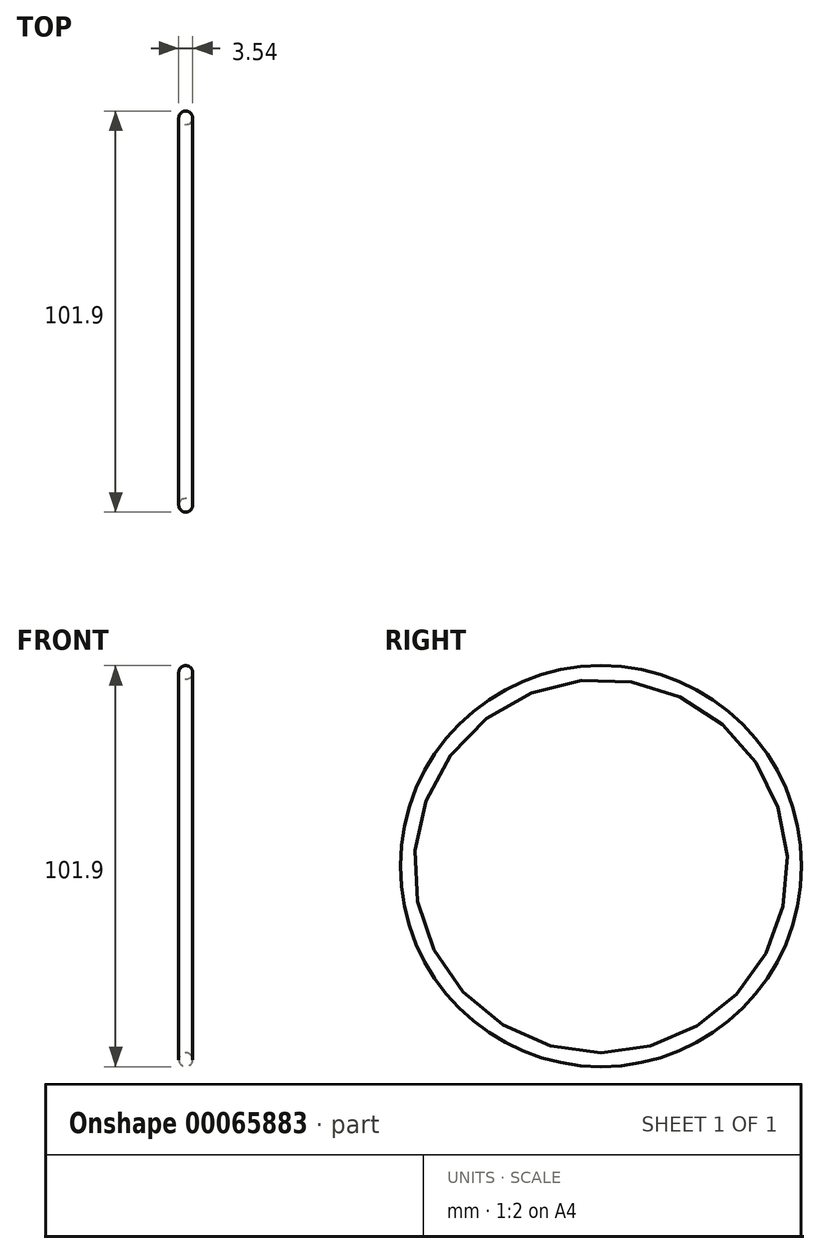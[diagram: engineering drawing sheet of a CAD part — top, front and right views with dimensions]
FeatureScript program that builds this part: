
annotation { "Feature Type Name" : "Feature", "Feature Type Description" : "" }
export const myFeature = defineFeature(function(context is Context, id is Id, definition is map)
    precondition{}
    {
        {
            var Q0;
            Q0=qCreatedBy(makeId("Front.planeOp"),FACE);
            var sketch = newSketch(context, id + "F0", { "sketchPlane" : qUnion([Q0])});
            skLineSegment(sketch, "E0", {"start": v(0, 0) * mm, "end": v(-6.06, 0) * mm, "construction": true});
            skCircle(sketch, "E1", {"center": v(0, 49.19) * mm, "radius": 1.77 * mm});
            skSolve(sketch);
        }
        {
            var Q0;
            Q0=makeQuery(id+"F0.imprint","IMPRINT",FACE,{"disambiguationData":[TD([[makeQuery(id+"F0.imprint","IMPRINT",EDGE,{"derivedFrom":sQuery(id+"F0.wireOp",EDGE,"E1")}),1.0]])]});
            var Q1;
            Q1=sQuery(id+"F0.wireOp",EDGE,"E0");
            revolve(context, id + "F1", {"entities" : qUnion([Q0]), "axis" : qUnion([Q1]), "revolveType" : RevolveType.FULL});
        }
    });
